# Revit family: Burko F-2850 Parallel
name_source: partatom
category: HLS-Bauteile
units: mm (PartAtom-declared; Revit-internal decimal feet)

## family parameters
Arbeitsebenenbasiert = Nein
Beim Laden mit Abzugskörper schneiden = Nein
Bemaßung runder Anschluss = Durchmesser verwenden
Beschriftungsausrichtung beibehalten = Nein
Gemeinsam genutzt = Nein
Immer vertikal = Ja
Klassifizierung = Keine
Raumberechnungspunkt = Nein
Teiletyp = Normal

## types (6) — shared parameters
Anschluss 1 1/2" = 40 mm  [stored 0.131234 ft]
Anschluss 1" = 25 mm  [stored 0.082021 ft]
Datenblatt = https://www.burkhalter-h2o.ch
Homepage = https://www.burkhalter-h2o.ch
LUT = LUT_Burko_F-2850
Steuerung_Höhe = 175 mm  [stored 0.574147 ft]
Steuerung_Tiefe = 75 mm  [stored 0.246063 ft]
zero-valued in all types: Vorgabe-Ansicht

## per-type parameters (varying)
| type | A | B | Behälterkopf | C | F | Harzinhalt_pro_Harzdruckbehälter | Sockel_Absatz_Oben | Sockel_Absatz_Unten | Sockel_Höhe | Steuerung_Breite |
| Burko F-2850 - 50 | 305 mm  [stored 1.00066 ft] | 1440 mm  [stored 4.72441 ft] | 100 mm  [stored 0.328084 ft] | 1305 mm  [stored 4.2815 ft] | 925 mm  [stored 3.03478 ft] | 50L | 163 mm | 163 mm | 100 mm  [stored 0.328084 ft] | 175 mm  [stored 0.574147 ft] |
| Burko F-2850 - 75L | 369 mm  [stored 1.21063 ft] | 1880 mm  [stored 6.16798 ft] | 150 mm  [stored 0.492126 ft] | 1740 mm  [stored 5.70866 ft] | 925 mm  [stored 3.03478 ft] | 75L | 195 mm  [stored 0.639764 ft] | 195 mm  [stored 0.639764 ft] | 100 mm  [stored 0.328084 ft] | 175 mm  [stored 0.574147 ft] |
| Burko F-2850 - 100L | 406 mm  [stored 1.33202 ft] | 1880 mm  [stored 6.16798 ft] | 150 mm  [stored 0.492126 ft] | 1740 mm  [stored 5.70866 ft] | 995 mm  [stored 3.26444 ft] | 100L | 213 mm  [stored 0.698819 ft] | 213 mm  [stored 0.698819 ft] | 100 mm  [stored 0.328084 ft] | 175 mm  [stored 0.574147 ft] |
| Burko F-2850 - 125L | 406 mm  [stored 1.33202 ft] | 1880 mm  [stored 6.16798 ft] | 150 mm  [stored 0.492126 ft] | 1740 mm  [stored 5.70866 ft] | 995 mm  [stored 3.26444 ft] | 125L | 213 mm  [stored 0.698819 ft] | 213 mm  [stored 0.698819 ft] | 150 mm  [stored 0.492126 ft] | 220 mm  [stored 0.721785 ft] |
| Burko F-2850 - 150L | 552 mm  [stored 1.81102 ft] | 1840 mm  [stored 6.03675 ft] | 200 mm  [stored 0.656168 ft] | 1700 mm  [stored 5.57743 ft] | 995 mm  [stored 3.26444 ft] | 150L | 286 mm  [stored 0.93832 ft] | 286 mm  [stored 0.93832 ft] | 150 mm  [stored 0.492126 ft] | 220 mm  [stored 0.721785 ft] |
| Burko F-2850 - 200L | 552 mm  [stored 1.81102 ft] | 1840 mm  [stored 6.03675 ft] | 200 mm  [stored 0.656168 ft] | 1700 mm  [stored 5.57743 ft] | 995 mm  [stored 3.26444 ft] | 200L | 286 mm  [stored 0.93832 ft] | 286 mm  [stored 0.93832 ft] | 150 mm  [stored 0.492126 ft] | 220 mm  [stored 0.721785 ft] |

note: [stored X ft] marks values corroborated as IEEE doubles in the binary element streams (Revit-internal decimal feet)
